# Revit family: ITK_Модуль Keystone Jack_90 градусов_Экранированный_IP20
name_source: partatom
category: Обобщенные модели
units: mm (PartAtom-declared; Revit-internal decimal feet)

## family parameters
Всегда вертикально = Да
Может служить основой для арматурных стержней = Нет
На основе рабочей плоскости = Нет
Общий = Нет
При загрузке вырезать с полостями = Нет
Размер круглого соединителя = Использовать диаметр
Тип детали = Нормальный
Точка расчета площади = Нет

## types (2) — shared parameters
ADSK_URL страницы изделия = https://www.itk-group.ru
ADSK_Версия Revit = 2019
ADSK_Версия семейства = 1.0
ADSK_Группирование = I. ЩИТЫ И ПУЛЬТЫ
ADSK_Единица измерения = шт
ADSK_Завод-изготовитель = IEK
ADSK_Материал наименование = Металл АБС-пластик
IEK_URL = https://www.itk-group.ru
IEK_Описание = Совместимость с компонентами для СКС.
Изготовлены из высококачественных негорючих материалов.
Надежность и удобство эксплуатации.
Соответствие международным стандартам качества
KSI_CMa_Строительные материалы = 01.7.14.03
URL = https://www.iek.ru
Высота = 22 мм
Глубина = 47 мм
Изготовитель = ITK
Материал = Нержавеющая сталь
Степень защиты = IP20
Ширина = 22 мм
zero-valued in all types: ADSK_Масса

## per-type parameters (varying)
| type | ADSK_Наименование | IEK_Цена за единицу |
| CS1-1C5EF-11 | ITK Модуль Keystone Jack кат. 5E FTP 110 IDC 90 град. розет. | 188.6 |
| CS1-1C06F-11 | ITK Модуль Keystone Jack кат. 6 FTP 110 IDC 90 град. розет. | 215.76 |

note: column(s) folded — value = type name in every type: ADSK_Код изделия
